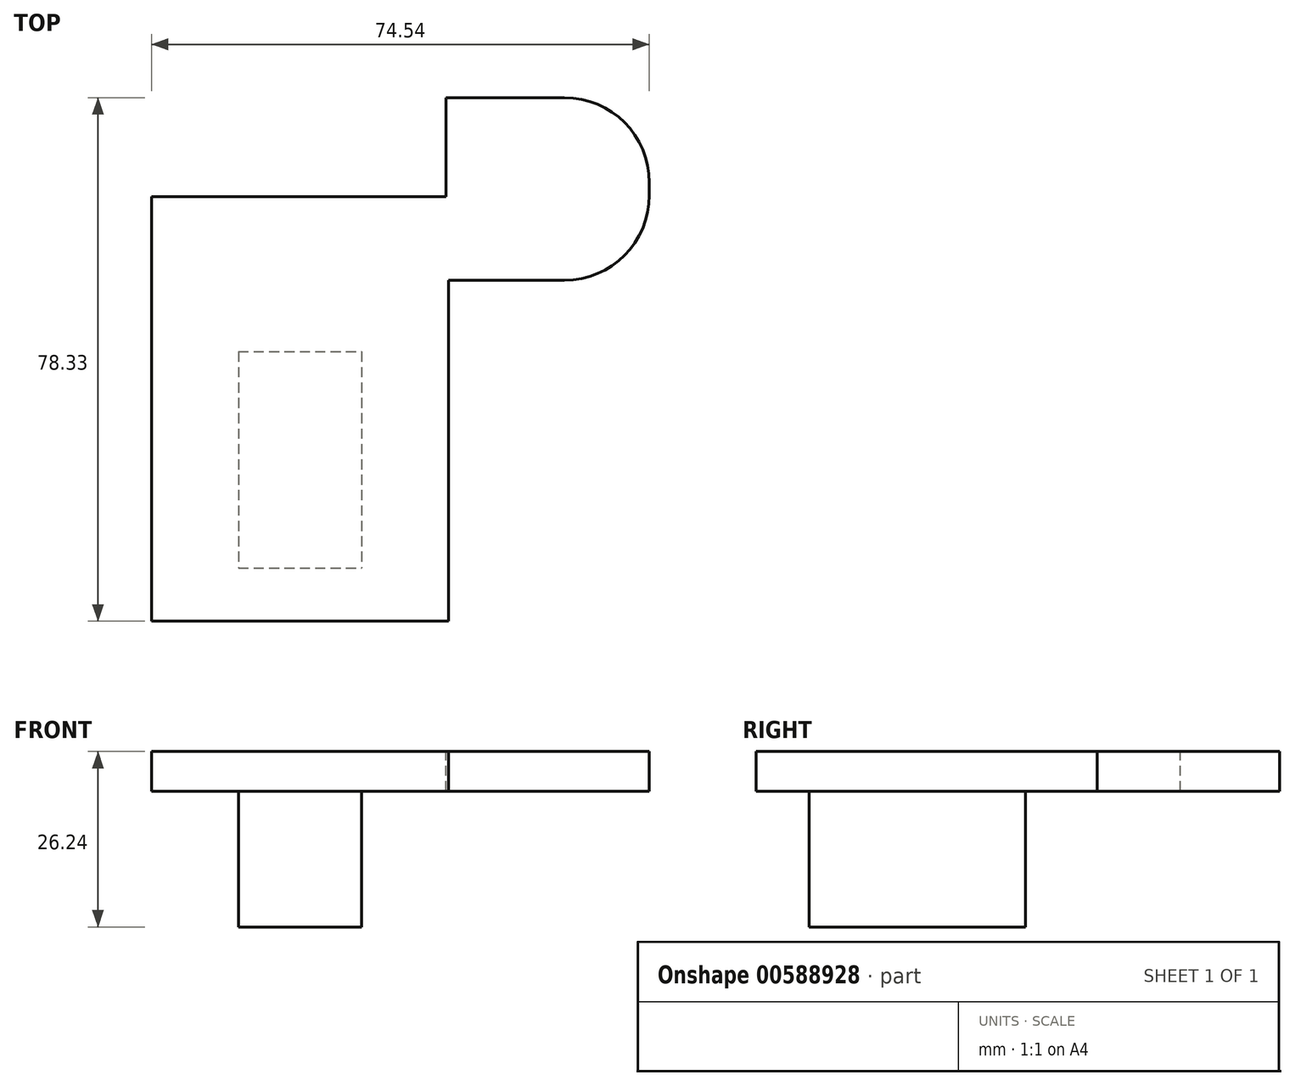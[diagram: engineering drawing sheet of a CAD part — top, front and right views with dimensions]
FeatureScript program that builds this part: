
annotation { "Feature Type Name" : "Feature", "Feature Type Description" : "" }
export const myFeature = defineFeature(function(context is Context, id is Id, definition is map)
    precondition{}
    {
        {
            var Q0;
            Q0=qCreatedBy(makeId("Top.planeOp"),FACE);
            var sketch = newSketch(context, id + "F0", { "sketchPlane" : qUnion([Q0])});
            skLineSegment(sketch, "E0.bottom", {"start": v(22.23, -62.23) * mm, "end": v(-22.22, -62.23) * mm});
            skLineSegment(sketch, "E0.top", {"start": v(22.23, 1.27) * mm, "end": v(-22.23, 1.27) * mm});
            skLineSegment(sketch, "E0.left", {"start": v(22.23, -62.23) * mm, "end": v(22.23, 1.27) * mm});
            skLineSegment(sketch, "E0.right", {"start": v(-22.22, -62.23) * mm, "end": v(-22.22, 1.27) * mm});
            skPoint(sketch, "E0.middle", {"position": v(0, -30.48) * mm});
            skPoint(sketch, "E1", {"position": v(-22.22, -62.23) * mm});
            skPoint(sketch, "E2", {"position": v(22.23, -62.23) * mm});
            skSolve(sketch);
        }
        {
            var Q0;
            Q0=qCreatedBy(makeId("Top.planeOp"),FACE);
            var sketch = newSketch(context, id + "F1", { "sketchPlane" : qUnion([Q0])});
            skLineSegment(sketch, "E3.bottom", {"start": v(21.88, 16.1) * mm, "end": v(39.61, 16.1) * mm});
            skLineSegment(sketch, "E3.top", {"start": v(21.88, -11.2) * mm, "end": v(39.61, -11.2) * mm});
            skLineSegment(sketch, "E3.left", {"start": v(21.88, 16.1) * mm, "end": v(21.88, -11.2) * mm});
            skLineSegment(sketch, "E3.right", {"start": v(52.31, 3.4) * mm, "end": v(52.31, 1.5) * mm});
            skPoint(sketch, "E4.visualSharp", {"position": v(52.31, -11.2) * mm});
            skArc(sketch, "E4.filletArc", {"start": v(39.61, -11.2) * mm, "mid": v(48.6, -7.49) * mm, "end": v(52.31, 1.5) * mm});
            skPoint(sketch, "E5.visualSharp", {"position": v(52.31, 16.1) * mm});
            skArc(sketch, "E5.filletArc", {"start": v(52.31, 3.4) * mm, "mid": v(48.6, 12.38) * mm, "end": v(39.61, 16.1) * mm});
            skSolve(sketch);
        }
        {
            var Q0;
            Q0=qSketchRegion(id+"F1",true);
            extrude(context, id + "F2", {"entities" : qUnion([Q0]), "depth" : 5.92 * mm, "offsetDistance" : 25.4 * mm});
        }
        {
            var Q0;
            Q0=makeQuery(id+"F0.imprint","IMPRINT",FACE,{"disambiguationData":[TD([[makeQuery(id+"F0.imprint","IMPRINT",EDGE,{"derivedFrom":sQuery(id+"F0.wireOp",EDGE,"E0.bottom")}),-1.0]])]});
            var Q1;
            Q1=makeQuery(id+"F2.opExtrude","CAP_FACE",FACE,{"disambiguationData":[OSD([sQuery(id+"F1.wireOp",EDGE,"E3.bottom"),sQuery(id+"F1.wireOp",EDGE,"E3.top"),sQuery(id+"F1.wireOp",EDGE,"E3.left"),sQuery(id+"F1.wireOp",EDGE,"E3.right"),sQuery(id+"F1.wireOp",EDGE,"E4.filletArc"),sQuery(id+"F1.wireOp",EDGE,"E5.filletArc")])],"isStart":true});
            extrude(context, id + "F3", {"entities" : qUnion([Q0, Q1]), "operationType" : NewBodyOperationType.ADD, "depth" : 5.92 * mm, "offsetDistance" : 25.4 * mm});
        }
        {
            var Q0;
            Q0=qCreatedBy(makeId("Top.planeOp"),FACE);
            var sketch = newSketch(context, id + "F4", { "sketchPlane" : qUnion([Q0])});
            skLineSegment(sketch, "E6.bottom", {"start": v(-9.2, -21.92) * mm, "end": v(9.2, -21.92) * mm});
            skLineSegment(sketch, "E6.top", {"start": v(-9.2, -54.3) * mm, "end": v(9.2, -54.3) * mm});
            skLineSegment(sketch, "E6.left", {"start": v(-9.2, -21.92) * mm, "end": v(-9.2, -54.3) * mm});
            skLineSegment(sketch, "E6.right", {"start": v(9.2, -21.92) * mm, "end": v(9.2, -54.3) * mm});
            skPoint(sketch, "E6.middle", {"position": v(0, -38.11) * mm});
            skSolve(sketch);
        }
        {
            var Q0;
            Q0=makeQuery(id+"F4.imprint","IMPRINT",FACE,{"disambiguationData":[TD([[makeQuery(id+"F4.imprint","IMPRINT",EDGE,{"derivedFrom":sQuery(id+"F4.wireOp",EDGE,"E6.bottom")}),-1.0]])]});
            extrude(context, id + "F5", {"entities" : qUnion([Q0]), "operationType" : NewBodyOperationType.ADD, "oppositeDirection" : true, "depth" : 20.32 * mm, "offsetDistance" : 25.4 * mm});
        }
    });
